# Revit family: Displays_Track_ASHanging_Contempo-Spacer
name_source: partatom
category: Generic Models
units: mm (PartAtom-declared; Revit-internal decimal feet)

## family parameters
Always vertical = No
Can host rebar = No
Classification Number = 23.40.90.11
Cut with Voids When Loaded = No
Maintain Annotation Orientation = No
Part Type = Normal
Room Calculation Point = No
Round Connector Dimension = Use Diameter
Shared = No
Work Plane-Based = Yes

## types (4) — shared parameters
Assembly Code = C1030500
Default Elevation = 4' - 0"
Description = AS Hanging Contempo Wall Track Spacer
Installation-Fabrication = https://www.ashanging.com
Keynote = 10 14 00
Manufacturer = AS Hanging
Manufacturer Website = https://www.ashanging.com
Model = Contempo Wall Track Spacer
Product Data = http://www.arcat.com
Product Properties = https://www.ashanging.com
Revision = R1_2017
Sales Information = https://www.ashanging.com
Specification = http://www.arcat.com
URL = https://www.ashanging.com

## type names (no varying parameters)
- Natural
- Champagne
- Black
- Silver Satin

note: column(s) folded — value = type name in every type: Finish

## geometry (parser evidence)
native form markers: Sweep x1
no freeform markers — native parametric forms only
